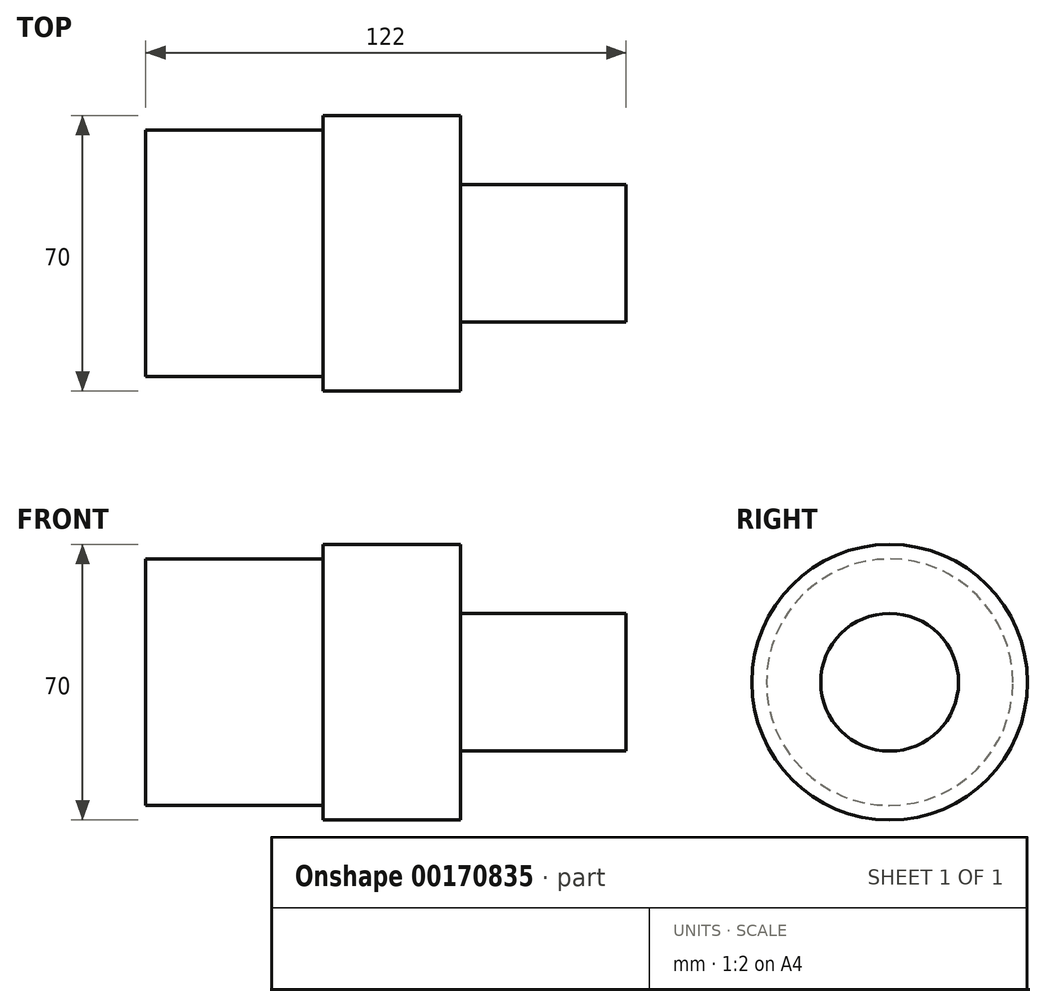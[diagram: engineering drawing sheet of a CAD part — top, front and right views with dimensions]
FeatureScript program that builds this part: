
annotation { "Feature Type Name" : "Feature", "Feature Type Description" : "" }
export const myFeature = defineFeature(function(context is Context, id is Id, definition is map)
    precondition{}
    {
        {
            var Q0;
            Q0=qCreatedBy(makeId("Top.planeOp"),FACE);
            var sketch = newSketch(context, id + "F0", { "sketchPlane" : qUnion([Q0])});
            skLineSegment(sketch, "E0", {"start": v(42, 0) * mm, "end": v(42, 17.5) * mm});
            skLineSegment(sketch, "E1", {"start": v(42, 17.5) * mm, "end": v(0, 17.5) * mm});
            skLineSegment(sketch, "E2", {"start": v(0, 17.5) * mm, "end": v(0, 35) * mm});
            skLineSegment(sketch, "E3", {"start": v(0, 35) * mm, "end": v(-35, 35) * mm});
            skLineSegment(sketch, "E4", {"start": v(-35, 35) * mm, "end": v(-35, 31.3) * mm});
            skLineSegment(sketch, "E5", {"start": v(-35, 31.3) * mm, "end": v(-80, 31.3) * mm});
            skLineSegment(sketch, "E6", {"start": v(-80, 31.3) * mm, "end": v(-80, 0) * mm});
            skLineSegment(sketch, "E7", {"start": v(-79.62, 0) * mm, "end": v(70.77, 0) * mm, "construction": true});
            skLineSegment(sketch, "E8", {"start": v(-80, 0) * mm, "end": v(42, 0) * mm});
            skSolve(sketch);
        }
        {
            var Q0;
            Q0 = qSketchRegion(id + "F0", true);
            var Q1;
            Q1=sQuery(id+"F0.wireOp",EDGE,"E7");
            revolve(context, id + "F1", {"entities" : qUnion([Q0]), "axis" : qUnion([Q1]), "revolveType" : RevolveType.FULL});
        }
    });
